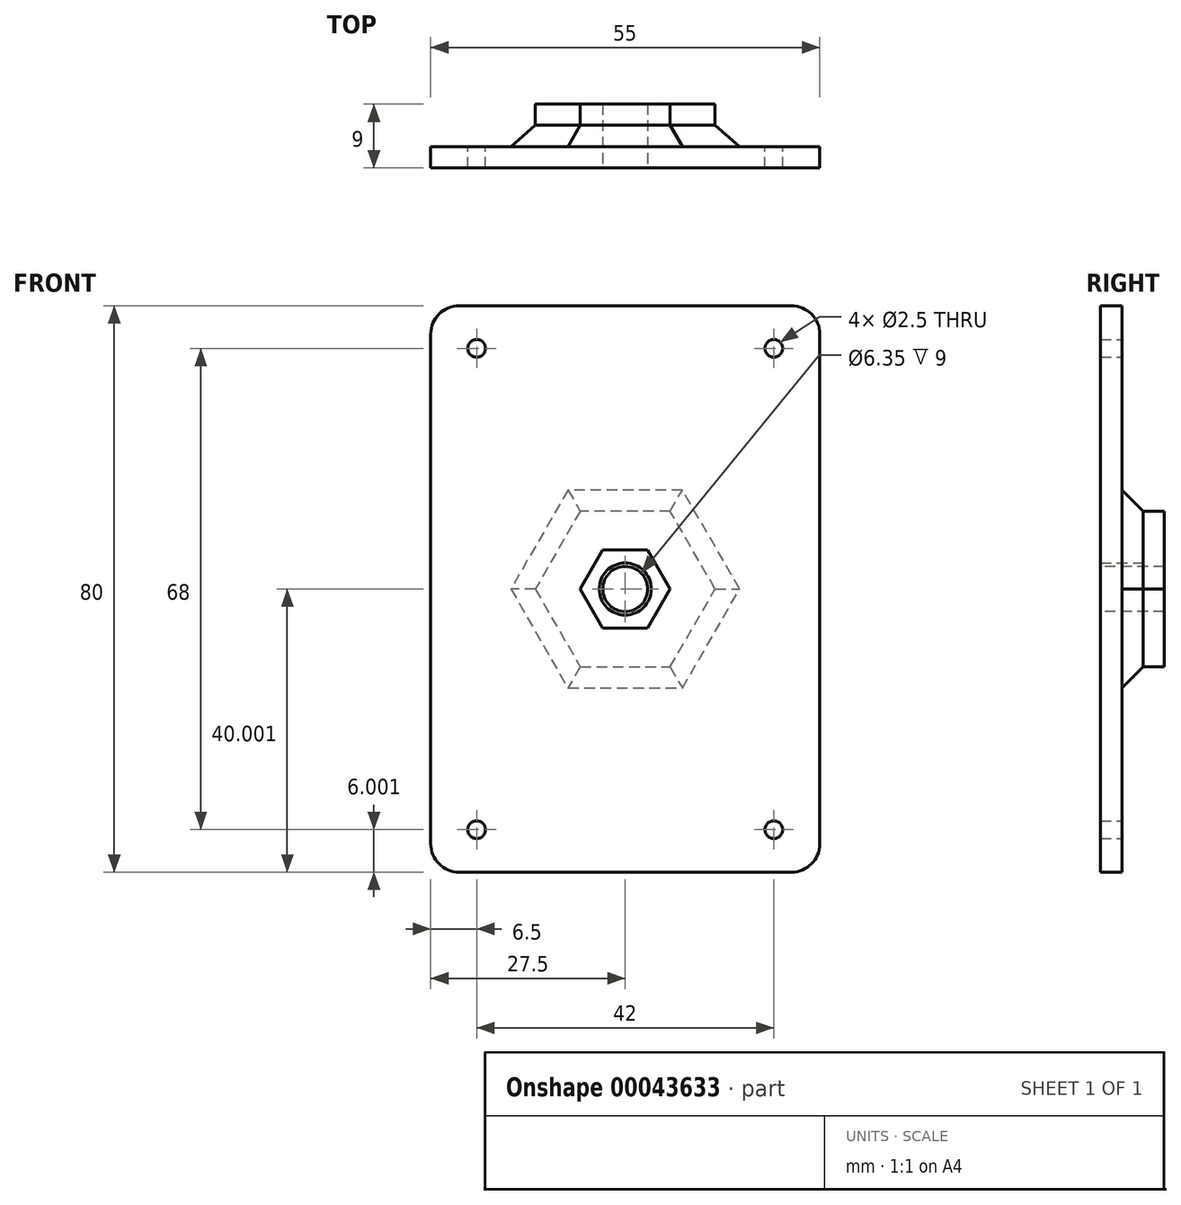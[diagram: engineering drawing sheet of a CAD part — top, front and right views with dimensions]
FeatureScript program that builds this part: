
annotation { "Feature Type Name" : "Feature", "Feature Type Description" : "" }
export const myFeature = defineFeature(function(context is Context, id is Id, definition is map)
    precondition{}
    {
        {
            var Q0;
            Q0=qCreatedBy(makeId("Front.planeOp"),FACE);
            var sketch = newSketch(context, id + "F0", { "sketchPlane" : qUnion([Q0])});
            skLineSegment(sketch, "E0.bottom", {"start": v(-21.59, 35.87) * mm, "end": v(20.41, 35.87) * mm, "construction": true});
            skLineSegment(sketch, "E0.top", {"start": v(-21.59, -32.13) * mm, "end": v(20.41, -32.13) * mm, "construction": true});
            skLineSegment(sketch, "E0.left", {"start": v(-21.59, 35.87) * mm, "end": v(-21.59, -32.13) * mm, "construction": true});
            skLineSegment(sketch, "E0.right", {"start": v(20.41, 35.87) * mm, "end": v(20.41, -32.13) * mm, "construction": true});
            skCircle(sketch, "E1", {"center": v(-21.59, 35.87) * mm, "radius": 1.25 * mm});
            skCircle(sketch, "E2", {"center": v(20.41, 35.87) * mm, "radius": 1.25 * mm});
            skCircle(sketch, "E3", {"center": v(20.41, -32.13) * mm, "radius": 1.25 * mm});
            skCircle(sketch, "E4", {"center": v(-21.59, -32.13) * mm, "radius": 1.25 * mm});
            skLineSegment(sketch, "E5.bottom", {"start": v(-24.09, 41.87) * mm, "end": v(22.91, 41.87) * mm});
            skLineSegment(sketch, "E5.top", {"start": v(-24.09, -38.13) * mm, "end": v(22.91, -38.13) * mm});
            skLineSegment(sketch, "E5.left", {"start": v(-28.09, 37.87) * mm, "end": v(-28.09, -34.13) * mm});
            skLineSegment(sketch, "E5.right", {"start": v(26.91, 37.87) * mm, "end": v(26.91, -34.13) * mm});
            skPoint(sketch, "E6.visualSharp", {"position": v(-28.09, 41.87) * mm});
            skArc(sketch, "E6.filletArc", {"start": v(-24.09, 41.87) * mm, "mid": v(-26.92, 40.7) * mm, "end": v(-28.09, 37.87) * mm});
            skPoint(sketch, "E7.visualSharp", {"position": v(26.91, 41.87) * mm});
            skArc(sketch, "E7.filletArc", {"start": v(26.91, 37.87) * mm, "mid": v(25.74, 40.7) * mm, "end": v(22.91, 41.87) * mm});
            skPoint(sketch, "E8.visualSharp", {"position": v(26.91, -38.13) * mm});
            skArc(sketch, "E8.filletArc", {"start": v(22.91, -38.13) * mm, "mid": v(25.74, -36.96) * mm, "end": v(26.91, -34.13) * mm});
            skPoint(sketch, "E9.visualSharp", {"position": v(-28.09, -38.13) * mm});
            skArc(sketch, "E9.filletArc", {"start": v(-28.09, -34.13) * mm, "mid": v(-26.92, -36.96) * mm, "end": v(-24.09, -38.13) * mm});
            skLineSegment(sketch, "E10", {"start": v(-21.59, 35.87) * mm, "end": v(20.41, -32.13) * mm, "construction": true});
            skCircle(sketch, "E11", {"center": v(-0.59, 1.87) * mm, "radius": 3.18 * mm});
            skCircle(sketch, "E12.cCircle", {"center": v(-0.59, 1.87) * mm, "radius": 5.5 * mm, "construction": true});
            skLineSegment(sketch, "E12.0", {"start": v(2.59, -3.63) * mm, "end": v(-3.77, -3.63) * mm});
            skLineSegment(sketch, "E12.1", {"start": v(-3.77, -3.63) * mm, "end": v(-6.94, 1.87) * mm});
            skLineSegment(sketch, "E12.2", {"start": v(-6.94, 1.87) * mm, "end": v(-3.77, 7.37) * mm});
            skLineSegment(sketch, "E12.3", {"start": v(-3.77, 7.37) * mm, "end": v(2.59, 7.37) * mm});
            skLineSegment(sketch, "E12.4", {"start": v(2.59, 7.37) * mm, "end": v(5.76, 1.87) * mm});
            skLineSegment(sketch, "E12.5", {"start": v(5.76, 1.87) * mm, "end": v(2.59, -3.63) * mm});
            skPoint(sketch, "E12.0.midPoint", {"position": v(-0.59, -3.63) * mm});
            skSolve(sketch);
        }
        {
            var Q0;
            Q0=makeQuery(id+"F0.imprint","IMPRINT",FACE,{"disambiguationData":[TD([[makeQuery(id+"F0.imprint","IMPRINT",EDGE,{"derivedFrom":sQuery(id+"F0.wireOp",EDGE,"E1")}),-1.0]])]});
            extrude(context, id + "F1", {"entities" : qUnion([Q0]), "depth" : 6 * mm});
        }
        {
            var Q0;
            Q0=makeQuery(id+"F1.opExtrude","CAP_FACE",FACE,{"disambiguationData":[OSD([sQuery(id+"F0.wireOp",EDGE,"E1"),sQuery(id+"F0.wireOp",EDGE,"E2"),sQuery(id+"F0.wireOp",EDGE,"E3"),sQuery(id+"F0.wireOp",EDGE,"E4"),sQuery(id+"F0.wireOp",EDGE,"E5.bottom"),sQuery(id+"F0.wireOp",EDGE,"E5.top"),sQuery(id+"F0.wireOp",EDGE,"E5.left"),sQuery(id+"F0.wireOp",EDGE,"E5.right"),sQuery(id+"F0.wireOp",EDGE,"E6.filletArc"),sQuery(id+"F0.wireOp",EDGE,"E7.filletArc"),sQuery(id+"F0.wireOp",EDGE,"E8.filletArc"),sQuery(id+"F0.wireOp",EDGE,"E9.filletArc"),sQuery(id+"F0.wireOp",EDGE,"E12.0"),sQuery(id+"F0.wireOp",EDGE,"E12.1"),sQuery(id+"F0.wireOp",EDGE,"E12.2"),sQuery(id+"F0.wireOp",EDGE,"E12.3"),sQuery(id+"F0.wireOp",EDGE,"E12.4"),sQuery(id+"F0.wireOp",EDGE,"E12.5")])],"isStart":true});
            var sketch = newSketch(context, id + "F2", { "sketchPlane" : qUnion([Q0])});
            skLineSegment(sketch, "E13", {"start": v(3.77, 7.37) * mm, "end": v(-2.59, -3.63) * mm, "construction": true});
            skCircle(sketch, "E14.cCircle", {"center": v(0.59, 1.87) * mm, "radius": 11 * mm, "construction": true});
            skLineSegment(sketch, "E14.0", {"start": v(6.94, -9.13) * mm, "end": v(-5.76, -9.13) * mm});
            skLineSegment(sketch, "E14.1", {"start": v(-5.76, -9.13) * mm, "end": v(-12.11, 1.87) * mm});
            skLineSegment(sketch, "E14.2", {"start": v(-12.11, 1.87) * mm, "end": v(-5.76, 12.87) * mm});
            skLineSegment(sketch, "E14.3", {"start": v(-5.76, 12.87) * mm, "end": v(6.94, 12.87) * mm});
            skLineSegment(sketch, "E14.4", {"start": v(6.94, 12.87) * mm, "end": v(13.3, 1.87) * mm});
            skLineSegment(sketch, "E14.5", {"start": v(13.3, 1.87) * mm, "end": v(6.94, -9.13) * mm});
            skPoint(sketch, "E14.0.midPoint", {"position": v(0.59, -9.13) * mm});
            skSolve(sketch);
        }
        {
            var Q0;
            Q0=makeQuery(id+"F2.imprint","IMPRINT",FACE,{"disambiguationData":[TD([[makeQuery(id+"F2.imprint","IMPRINT",EDGE,{"derivedFrom":sQuery(id+"F2.wireOp",EDGE,"E14.0")}),1.0]])]});
            extrude(context, id + "F3", {"entities" : qUnion([Q0]), "operationType" : NewBodyOperationType.REMOVE, "oppositeDirection" : true, "depth" : 3 * mm});
        }
        {
            var Q0;
            Q0=makeQuery(id+"F3.boolean.opBoolean","COPY",EDGE,{"derivedFrom":makeQuery(id+"F3.opExtrude","CAP_EDGE",EDGE,{"disambiguationData":[OSD([sQuery(id+"F2.wireOp",EDGE,"E14.2")])],"isStart":false})});
            var Q1;
            Q1=makeQuery(id+"F3.boolean.opBoolean","COPY",EDGE,{"derivedFrom":makeQuery(id+"F3.opExtrude","CAP_EDGE",EDGE,{"disambiguationData":[OSD([sQuery(id+"F2.wireOp",EDGE,"E14.1")])],"isStart":false})});
            var Q2;
            Q2=makeQuery(id+"F3.boolean.opBoolean","COPY",EDGE,{"derivedFrom":makeQuery(id+"F3.opExtrude","CAP_EDGE",EDGE,{"disambiguationData":[OSD([sQuery(id+"F2.wireOp",EDGE,"E14.0")])],"isStart":false})});
            var Q3;
            Q3=makeQuery(id+"F3.boolean.opBoolean","COPY",EDGE,{"derivedFrom":makeQuery(id+"F3.opExtrude","CAP_EDGE",EDGE,{"disambiguationData":[OSD([sQuery(id+"F2.wireOp",EDGE,"E14.5")])],"isStart":false})});
            var Q4;
            Q4=makeQuery(id+"F3.boolean.opBoolean","COPY",EDGE,{"derivedFrom":makeQuery(id+"F3.opExtrude","CAP_EDGE",EDGE,{"disambiguationData":[OSD([sQuery(id+"F2.wireOp",EDGE,"E14.4")])],"isStart":false})});
            var Q5;
            Q5=makeQuery(id+"F3.boolean.opBoolean","COPY",EDGE,{"derivedFrom":makeQuery(id+"F3.opExtrude","CAP_EDGE",EDGE,{"disambiguationData":[OSD([sQuery(id+"F2.wireOp",EDGE,"E14.3")])],"isStart":false})});
            chamfer(context, id + "F4", {"entities" : qUnion([Q0, Q1, Q2, Q3, Q4, Q5]), "width" : 3 * mm, "tangentPropagation" : true});
        }
        {
            var Q0;
            Q0=makeQuery(id+"F1.opExtrude","CAP_FACE",FACE,{"disambiguationData":[OSD([sQuery(id+"F0.wireOp",EDGE,"E1"),sQuery(id+"F0.wireOp",EDGE,"E2"),sQuery(id+"F0.wireOp",EDGE,"E3"),sQuery(id+"F0.wireOp",EDGE,"E4"),sQuery(id+"F0.wireOp",EDGE,"E5.bottom"),sQuery(id+"F0.wireOp",EDGE,"E5.top"),sQuery(id+"F0.wireOp",EDGE,"E5.left"),sQuery(id+"F0.wireOp",EDGE,"E5.right"),sQuery(id+"F0.wireOp",EDGE,"E6.filletArc"),sQuery(id+"F0.wireOp",EDGE,"E7.filletArc"),sQuery(id+"F0.wireOp",EDGE,"E8.filletArc"),sQuery(id+"F0.wireOp",EDGE,"E9.filletArc"),sQuery(id+"F0.wireOp",EDGE,"E12.0"),sQuery(id+"F0.wireOp",EDGE,"E12.1"),sQuery(id+"F0.wireOp",EDGE,"E12.2"),sQuery(id+"F0.wireOp",EDGE,"E12.3"),sQuery(id+"F0.wireOp",EDGE,"E12.4"),sQuery(id+"F0.wireOp",EDGE,"E12.5")])],"isStart":true});
            var sketch = newSketch(context, id + "F5", { "sketchPlane" : qUnion([Q0])});
            skLineSegment(sketch, "E15", {"start": v(-5.76, 12.87) * mm, "end": v(6.94, -9.13) * mm, "construction": true});
            skCircle(sketch, "E16", {"center": v(0.59, 1.87) * mm, "radius": 3.18 * mm});
            skSolve(sketch);
        }
        {
            var Q0;
            {var subQ0=sQuery(id+"F0.wireOp",EDGE,"E12.0");Q0=makeQuery(id+"F5.imprint","IMPRINT",FACE,{"disambiguationData":[TD([[makeQuery(id+"F5.imprint","IMPRINT",EDGE,{"derivedFrom":makeQuery(id+"F1.opExtrude","CAP_EDGE",EDGE,{"disambiguationData":[OSD([subQ0])],"isStart":true})}),-1.0]])]});}
            var Q1;
            Q1=makeQuery(id+"F5.imprint","IMPRINT",FACE,{"disambiguationData":[TD([[makeQuery(id+"F5.imprint","IMPRINT",EDGE,{"derivedFrom":sQuery(id+"F5.wireOp",EDGE,"E16")}),-1.0]])]});
            extrude(context, id + "F6", {"entities" : qUnion([Q0, Q1]), "operationType" : NewBodyOperationType.ADD, "depth" : 3 * mm});
        }
        {
            var Q0;
            Q0=makeQuery(id+"F6.opExtrude","CAP_FACE",FACE,{"disambiguationData":[OSD([sQuery(id+"F0.wireOp",EDGE,"E1"),sQuery(id+"F0.wireOp",EDGE,"E2"),sQuery(id+"F0.wireOp",EDGE,"E3"),sQuery(id+"F0.wireOp",EDGE,"E4"),sQuery(id+"F0.wireOp",EDGE,"E5.bottom"),sQuery(id+"F0.wireOp",EDGE,"E5.top"),sQuery(id+"F0.wireOp",EDGE,"E5.left"),sQuery(id+"F0.wireOp",EDGE,"E5.right"),sQuery(id+"F0.wireOp",EDGE,"E6.filletArc"),sQuery(id+"F0.wireOp",EDGE,"E7.filletArc"),sQuery(id+"F0.wireOp",EDGE,"E8.filletArc"),sQuery(id+"F0.wireOp",EDGE,"E9.filletArc"),sQuery(id+"F0.wireOp",EDGE,"E12.0"),sQuery(id+"F0.wireOp",EDGE,"E12.1"),sQuery(id+"F0.wireOp",EDGE,"E12.2"),sQuery(id+"F0.wireOp",EDGE,"E12.3"),sQuery(id+"F0.wireOp",EDGE,"E12.4"),sQuery(id+"F0.wireOp",EDGE,"E12.5"),sQuery(id+"F2.wireOp",EDGE,"E14.0"),sQuery(id+"F2.wireOp",EDGE,"E14.1"),sQuery(id+"F2.wireOp",EDGE,"E14.2"),sQuery(id+"F2.wireOp",EDGE,"E14.3"),sQuery(id+"F2.wireOp",EDGE,"E14.4"),sQuery(id+"F2.wireOp",EDGE,"E14.5"),sQuery(id+"F5.wireOp",EDGE,"E16")])],"isStart":true});
            var sketch = newSketch(context, id + "F7", { "sketchPlane" : qUnion([Q0])});
            skCircle(sketch, "E17", {"center": v(-0.59, 1.87) * mm, "radius": 3.68 * mm});
            skSolve(sketch);
        }
        {
            var Q0;
            Q0=makeQuery(id+"F7.imprint","IMPRINT",FACE,{"disambiguationData":[TD([[makeQuery(id+"F7.imprint","IMPRINT",EDGE,{"derivedFrom":sQuery(id+"F7.wireOp",EDGE,"E17")}),1.0]])]});
            var Q1;
            Q1=makeQuery(id+"F1.opExtrude","CAP_FACE",FACE,{"disambiguationData":[OSD([sQuery(id+"F0.wireOp",EDGE,"E1"),sQuery(id+"F0.wireOp",EDGE,"E2"),sQuery(id+"F0.wireOp",EDGE,"E3"),sQuery(id+"F0.wireOp",EDGE,"E4"),sQuery(id+"F0.wireOp",EDGE,"E5.bottom"),sQuery(id+"F0.wireOp",EDGE,"E5.top"),sQuery(id+"F0.wireOp",EDGE,"E5.left"),sQuery(id+"F0.wireOp",EDGE,"E5.right"),sQuery(id+"F0.wireOp",EDGE,"E6.filletArc"),sQuery(id+"F0.wireOp",EDGE,"E7.filletArc"),sQuery(id+"F0.wireOp",EDGE,"E8.filletArc"),sQuery(id+"F0.wireOp",EDGE,"E9.filletArc"),sQuery(id+"F0.wireOp",EDGE,"E12.0"),sQuery(id+"F0.wireOp",EDGE,"E12.1"),sQuery(id+"F0.wireOp",EDGE,"E12.2"),sQuery(id+"F0.wireOp",EDGE,"E12.3"),sQuery(id+"F0.wireOp",EDGE,"E12.4"),sQuery(id+"F0.wireOp",EDGE,"E12.5")])],"isStart":false});
            extrude(context, id + "F8", {"entities" : qUnion([Q0]), "operationType" : NewBodyOperationType.ADD, "endBound" : BoundingType.UP_TO_SURFACE, "endBoundEntityFace" : qUnion([Q1]), "depth" : 25.4 * mm});
        }
    });
